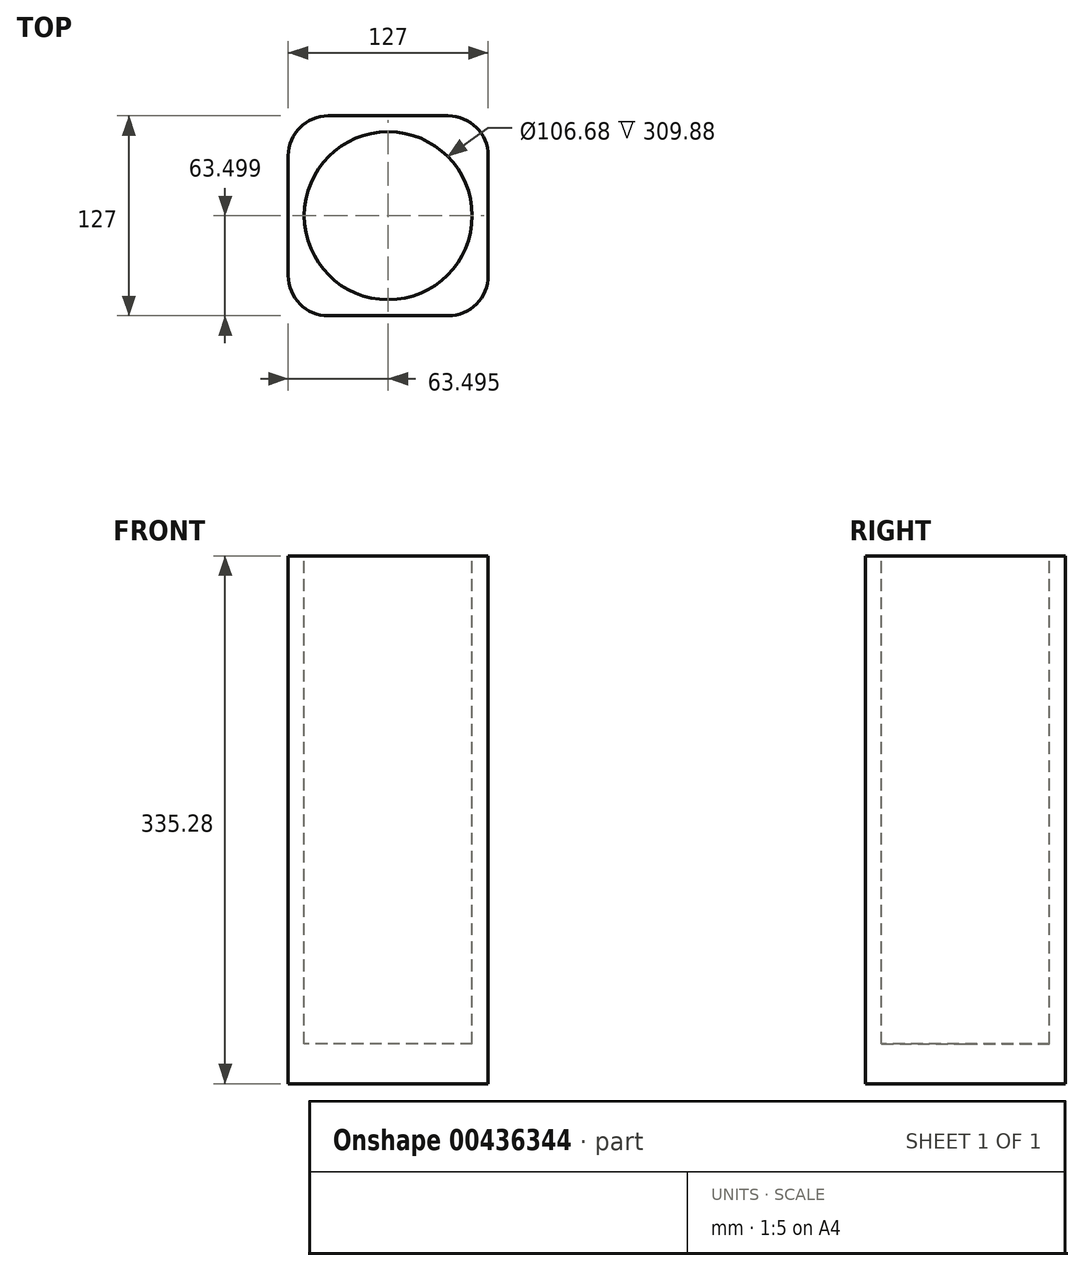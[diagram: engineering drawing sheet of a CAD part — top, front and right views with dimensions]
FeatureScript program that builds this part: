
annotation { "Feature Type Name" : "Feature", "Feature Type Description" : "" }
export const myFeature = defineFeature(function(context is Context, id is Id, definition is map)
    precondition{}
    {
        {
            var Q0;
            Q0=qCreatedBy(makeId("Top.planeOp"),FACE);
            var sketch = newSketch(context, id + "F0", { "sketchPlane" : qUnion([Q0])});
            skLineSegment(sketch, "E0.bottom", {"start": v(-146.67, 59.12) * mm, "end": v(-19.67, 59.12) * mm});
            skLineSegment(sketch, "E0.top", {"start": v(-146.67, -67.88) * mm, "end": v(-19.67, -67.88) * mm});
            skLineSegment(sketch, "E0.left", {"start": v(-146.67, 59.12) * mm, "end": v(-146.67, -67.88) * mm});
            skLineSegment(sketch, "E0.right", {"start": v(-19.67, 59.12) * mm, "end": v(-19.67, -67.88) * mm});
            skSolve(sketch);
        }
        {
            var Q0;
            Q0 = qSketchRegion(id + "F0", true);
            extrude(context, id + "F1", {"entities" : qUnion([Q0]), "depth" : 335.28 * mm});
        }
        {
            var Q0;
            Q0=makeQuery(id+"F1.opExtrude","CAP_FACE",FACE,{"disambiguationData":[OSD([sQuery(id+"F0.wireOp",EDGE,"E0.bottom"),sQuery(id+"F0.wireOp",EDGE,"E0.top"),sQuery(id+"F0.wireOp",EDGE,"E0.left"),sQuery(id+"F0.wireOp",EDGE,"E0.right")])],"isStart":false});
            var sketch = newSketch(context, id + "F2", { "sketchPlane" : qUnion([Q0])});
            skCircle(sketch, "E1", {"center": v(-83.17, -4.38) * mm, "radius": 53.34 * mm});
            skSolve(sketch);
        }
        {
            var Q0;
            Q0 = qSketchRegion(id + "F2", true);
            extrude(context, id + "F3", {"entities" : qUnion([Q0]), "operationType" : NewBodyOperationType.REMOVE, "oppositeDirection" : true, "depth" : 309.88 * mm});
        }
        {
            var Q0;
            Q0=makeQuery(id+"F1.opExtrude","SWEPT_EDGE",EDGE,{"disambiguationData":[OSD([sQuery(id+"F0.wireOp",EDGE,"E0.bottom"),sQuery(id+"F0.wireOp",EDGE,"E0.right")])]});
            var Q1;
            Q1=makeQuery(id+"F1.opExtrude","SWEPT_EDGE",EDGE,{"disambiguationData":[OSD([sQuery(id+"F0.wireOp",EDGE,"E0.bottom"),sQuery(id+"F0.wireOp",EDGE,"E0.left")])]});
            var Q2;
            Q2=makeQuery(id+"F1.opExtrude","SWEPT_EDGE",EDGE,{"disambiguationData":[OSD([sQuery(id+"F0.wireOp",EDGE,"E0.top"),sQuery(id+"F0.wireOp",EDGE,"E0.left")])]});
            var Q3;
            Q3=makeQuery(id+"F1.opExtrude","SWEPT_EDGE",EDGE,{"disambiguationData":[OSD([sQuery(id+"F0.wireOp",EDGE,"E0.top"),sQuery(id+"F0.wireOp",EDGE,"E0.right")])]});
            fillet(context, id + "F4", {"entities" : qUnion([Q0, Q1, Q2, Q3]), "radius" : 25.4 * mm, "tangentPropagation" : true, "allowEdgeOverflow" : false});
        }
    });
